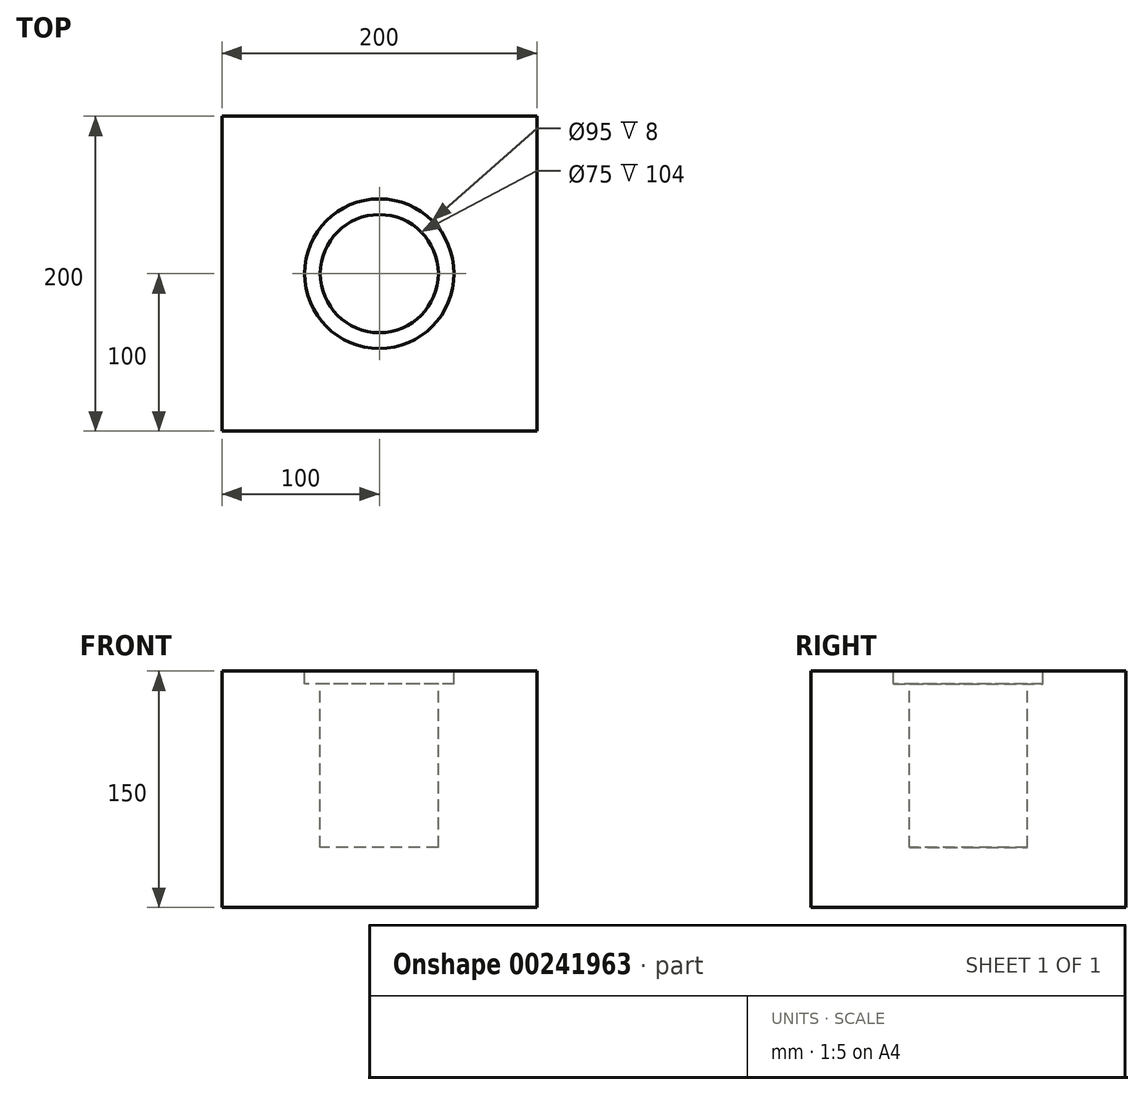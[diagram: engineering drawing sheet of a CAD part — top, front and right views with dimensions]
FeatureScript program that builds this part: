
annotation { "Feature Type Name" : "Feature", "Feature Type Description" : "" }
export const myFeature = defineFeature(function(context is Context, id is Id, definition is map)
    precondition{}
    {
        {
            var Q0;
            Q0=qCreatedBy(makeId("Top.planeOp"),FACE);
            var sketch = newSketch(context, id + "F0", { "sketchPlane" : qUnion([Q0])});
            skLineSegment(sketch, "E0.bottom", {"start": v(-100, 100) * mm, "end": v(100, 100) * mm});
            skLineSegment(sketch, "E0.top", {"start": v(-100, -100) * mm, "end": v(100, -100) * mm});
            skLineSegment(sketch, "E0.left", {"start": v(-100, 100) * mm, "end": v(-100, -100) * mm});
            skLineSegment(sketch, "E0.right", {"start": v(100, 100) * mm, "end": v(100, -100) * mm});
            skPoint(sketch, "E1", {"position": v(0, 100) * mm});
            skPoint(sketch, "E2", {"position": v(-100, 0) * mm});
            skSolve(sketch);
        }
        {
            var Q0;
            Q0 = qSketchRegion(id + "F0", true);
            extrude(context, id + "F1", {"entities" : qUnion([Q0]), "depth" : 150 * mm});
        }
        {
            var Q0;
            Q0=makeQuery(id+"F1.opExtrude","CAP_FACE",FACE,{"disambiguationData":[OSD([sQuery(id+"F0.wireOp",EDGE,"E0.bottom"),sQuery(id+"F0.wireOp",EDGE,"E0.top"),sQuery(id+"F0.wireOp",EDGE,"E0.left"),sQuery(id+"F0.wireOp",EDGE,"E0.right")])],"isStart":false});
            var sketch = newSketch(context, id + "F2", { "sketchPlane" : qUnion([Q0])});
            skCircle(sketch, "E3", {"center": v(0, 0) * mm, "radius": 37.5 * mm});
            skSolve(sketch);
        }
        {
            var Q0;
            Q0 = qSketchRegion(id + "F2", true);
            extrude(context, id + "F3", {"entities" : qUnion([Q0]), "operationType" : NewBodyOperationType.REMOVE, "oppositeDirection" : true, "depth" : 112 * mm});
        }
        {
            var Q0;
            Q0=makeQuery(id+"F1.opExtrude","CAP_FACE",FACE,{"disambiguationData":[OSD([sQuery(id+"F0.wireOp",EDGE,"E0.bottom"),sQuery(id+"F0.wireOp",EDGE,"E0.top"),sQuery(id+"F0.wireOp",EDGE,"E0.left"),sQuery(id+"F0.wireOp",EDGE,"E0.right")])],"isStart":false});
            var sketch = newSketch(context, id + "F4", { "sketchPlane" : qUnion([Q0])});
            skCircle(sketch, "E4", {"center": v(0, 0) * mm, "radius": 47.5 * mm});
            skSolve(sketch);
        }
        {
            var Q0;
            Q0 = qSketchRegion(id + "F4", true);
            extrude(context, id + "F5", {"entities" : qUnion([Q0]), "operationType" : NewBodyOperationType.REMOVE, "oppositeDirection" : true, "depth" : 8 * mm});
        }
    });
